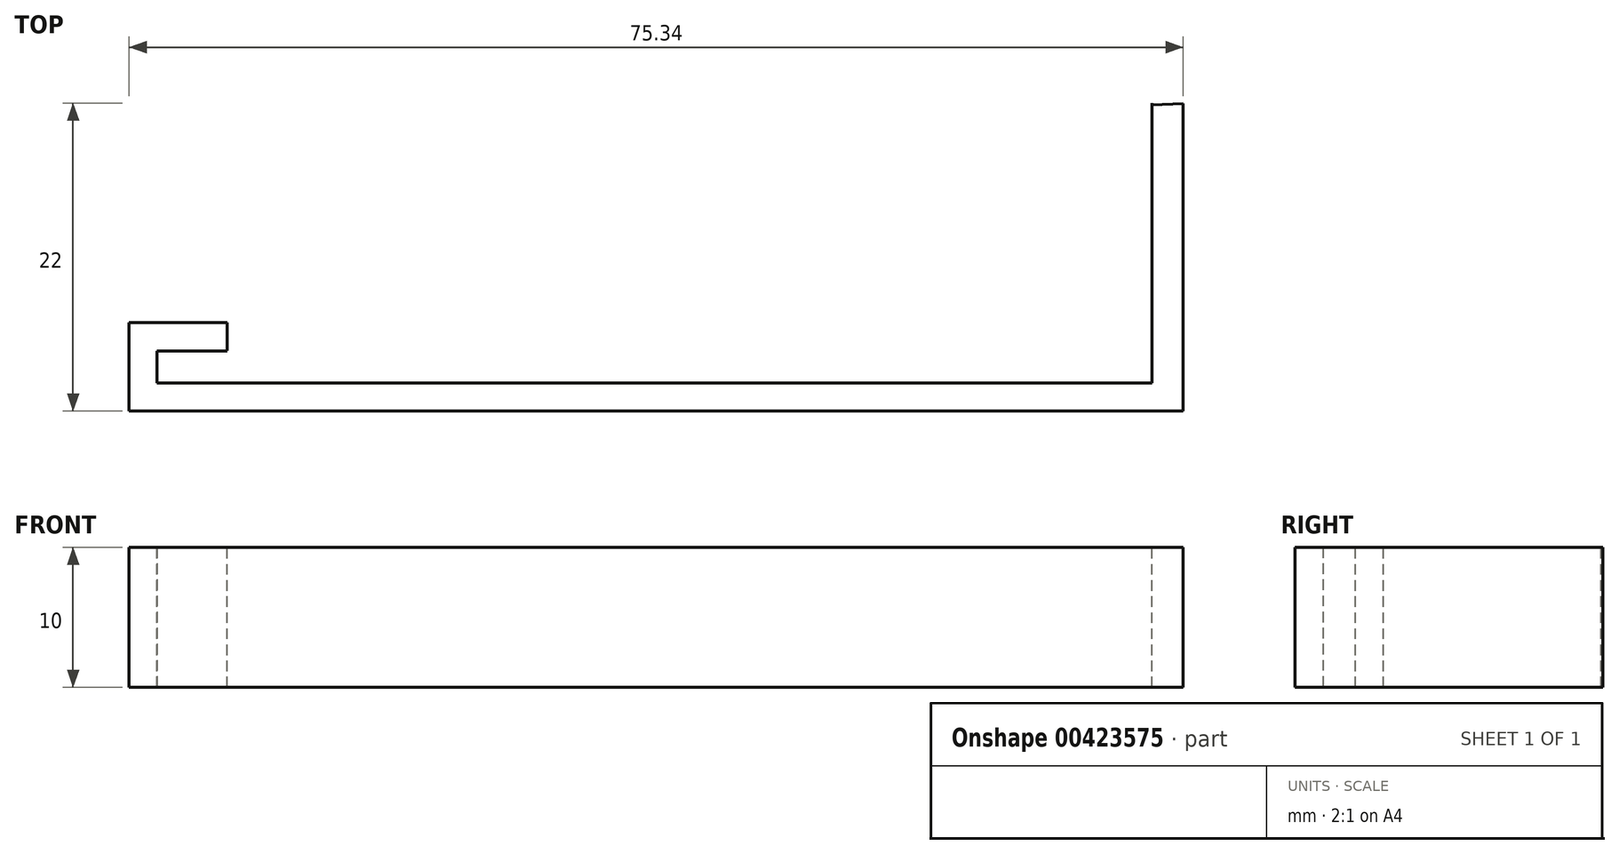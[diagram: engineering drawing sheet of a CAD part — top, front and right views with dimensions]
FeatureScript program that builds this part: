
annotation { "Feature Type Name" : "Feature", "Feature Type Description" : "" }
export const myFeature = defineFeature(function(context is Context, id is Id, definition is map)
    precondition{}
    {
        {
            var Q0;
            Q0=qCreatedBy(makeId("Top.planeOp"),FACE);
            var sketch = newSketch(context, id + "F0", { "sketchPlane" : qUnion([Q0])});
            skLineSegment(sketch, "E0", {"start": v(-39.7, 0) * mm, "end": v(31.4, 0) * mm});
            skSolve(sketch);
        }
        {
            var Q0;
            Q0=qCreatedBy(makeId("Top.planeOp"),FACE);
            var sketch = newSketch(context, id + "F1", { "sketchPlane" : qUnion([Q0])});
            skLineSegment(sketch, "E1", {"start": v(-39.69, 0) * mm, "end": v(-39.69, 2.3) * mm});
            skLineSegment(sketch, "E2", {"start": v(-39.69, 2.3) * mm, "end": v(-34.69, 2.3) * mm});
            skLineSegment(sketch, "E3", {"start": v(31.42, 0) * mm, "end": v(31.42, 20) * mm});
            skSolve(sketch);
        }
        {
            var Q0;
            Q0=qCreatedBy(makeId("Top.planeOp"),FACE);
            var sketch = newSketch(context, id + "F2", { "sketchPlane" : qUnion([Q0])});
            skLineSegment(sketch, "E4", {"start": v(-34.7, 2.31) * mm, "end": v(-34.7, 4.31) * mm});
            skLineSegment(sketch, "E5", {"start": v(-34.7, 4.31) * mm, "end": v(-41.69, 4.31) * mm});
            skLineSegment(sketch, "E6", {"start": v(-41.69, 4.31) * mm, "end": v(-41.69, -2) * mm});
            skLineSegment(sketch, "E7", {"start": v(-41.69, -2) * mm, "end": v(33.65, -2) * mm});
            skLineSegment(sketch, "E8", {"start": v(33.65, -2) * mm, "end": v(33.65, 19.99) * mm});
            skLineSegment(sketch, "E9", {"start": v(33.65, 19.99) * mm, "end": v(31.44, 19.88) * mm});
            skSolve(sketch);
        }
        {
            var Q0;
            Q0=sQuery(id+"F0.wireOp",EDGE,"E0");
            var Q1;
            Q1=sQuery(id+"F1.wireOp",EDGE,"E1");
            var Q2;
            Q2=sQuery(id+"F1.wireOp",EDGE,"E2");
            var Q3;
            Q3=sQuery(id+"F1.wireOp",EDGE,"E3");
            var Q4;
            Q4=sQuery(id+"F2.wireOp",EDGE,"E9");
            var Q5;
            Q5=sQuery(id+"F2.wireOp",EDGE,"E6");
            var Q6;
            Q6=sQuery(id+"F2.wireOp",EDGE,"E4");
            var Q7;
            Q7=sQuery(id+"F2.wireOp",EDGE,"E8");
            var Q8;
            Q8=sQuery(id+"F2.wireOp",EDGE,"E7");
            var Q9;
            Q9=sQuery(id+"F2.wireOp",EDGE,"E5");
            extrude(context, id + "F3", {"bodyType" : ToolBodyType.SURFACE, "surfaceEntities" : qUnion([Q0, Q1, Q2, Q3, Q4, Q5, Q6, Q7, Q8, Q9]), "depth" : 10 * mm});
        }
    });
